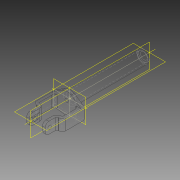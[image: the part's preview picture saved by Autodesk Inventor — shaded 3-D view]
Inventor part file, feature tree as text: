
AUTODESK INVENTOR PART (.ipt)
format: ipt  version: 2015 (Build 190159000, 159)  size: 218,624 bytes
history: native  units: mm
features: sketch x7, projected_geometry x4, extrude x3, chamfer x2, plane x2, fillet x2, shell x1, sweep x1, loft x1, mirror x1, hole x1
ambient origin geometry x8: Origin, YZ Plane, XZ Plane, XY Plane, X Axis, Y Axis, Z Axis, Center Point
bodies: Solid1 (feature_tree)
feature tree (25):
  extrude  "Extrusion1"  Depth=165.0mm TaperAngle=0.0deg
  chamfer  "Chamfer1"  Distance=2.0mm Angle=45.0deg
  shell  "Shell1"  Thickness=3.0mm
  extrude  "Extrusion2"  Depth=32.5mm
  plane  "Work Plane1"
  sweep  "Sweep1"
  fillet  "Fillet1"  Radius=32.5mm
  fillet  "Fillet2"  Radius=7.0mm
  plane  "Work Plane2"
  sketch  "Sketch5"  dims[d17=12.0mm d18=26.0mm]
  loft  "Loft1"
  extrude  "Extrusion3"  Depth=26.0mm
  mirror  "Mirror1"
  hole  "Hole1"  [1 undecoded]
  chamfer  "Chamfer2"  [1 undecoded]
  sketch  "Sketch1"  dims[d0=28.0mm d1=165.0mm d2=0.0mm d3=2.0mm d4=2.0mm d5=45.0deg d6=3.0mm]
  sketch  "Sketch2"  dims[d7=36.0mm d8=32.5mm]
  sketch  "Sketch3"  dims[d9=25.0mm d10=30.0mm d11=32.5mm d12=7.0mm d13=0.0mm]
  projected_geometry  "Projected Loop1"
  sketch  "Sketch4"  dims[d14=6.0mm d16=42.0mm]
  projected_geometry  "Projected Loop2"
  sketch  "Sketch6"  dims[d19=7.5mm d20=3.5mm d21=0.0mm d22=0.0mm]
  projected_geometry  "Projected Loop3"
  sketch  "Sketch7"  dims[d23=6.0mm d24=8.0mm d25=2.5mm d26=8.0mm d27=10.0mm d28=10.0mm d29=10.0mm d30=10.0mm d31=20.0mm d32=2.0mm d33=0.0mm d34=90.0deg d35=0.0mm d36=90.0deg d37=7.0mm d38=0.0mm d39=8.0mm d40=6.0mm d41=4.0mm d42=2.0mm d43=90.0deg d44=8.0mm d45=20.594885mm d46=2.0mm d47=2.0mm d48=45.0deg]
  projected_geometry  "Projected Loop4"
note: 2 required parameter values undecoded (feature->parameter linkage not recoverable at this tier; creation-order binding heuristic only, values carry confidence <= 0.55)
